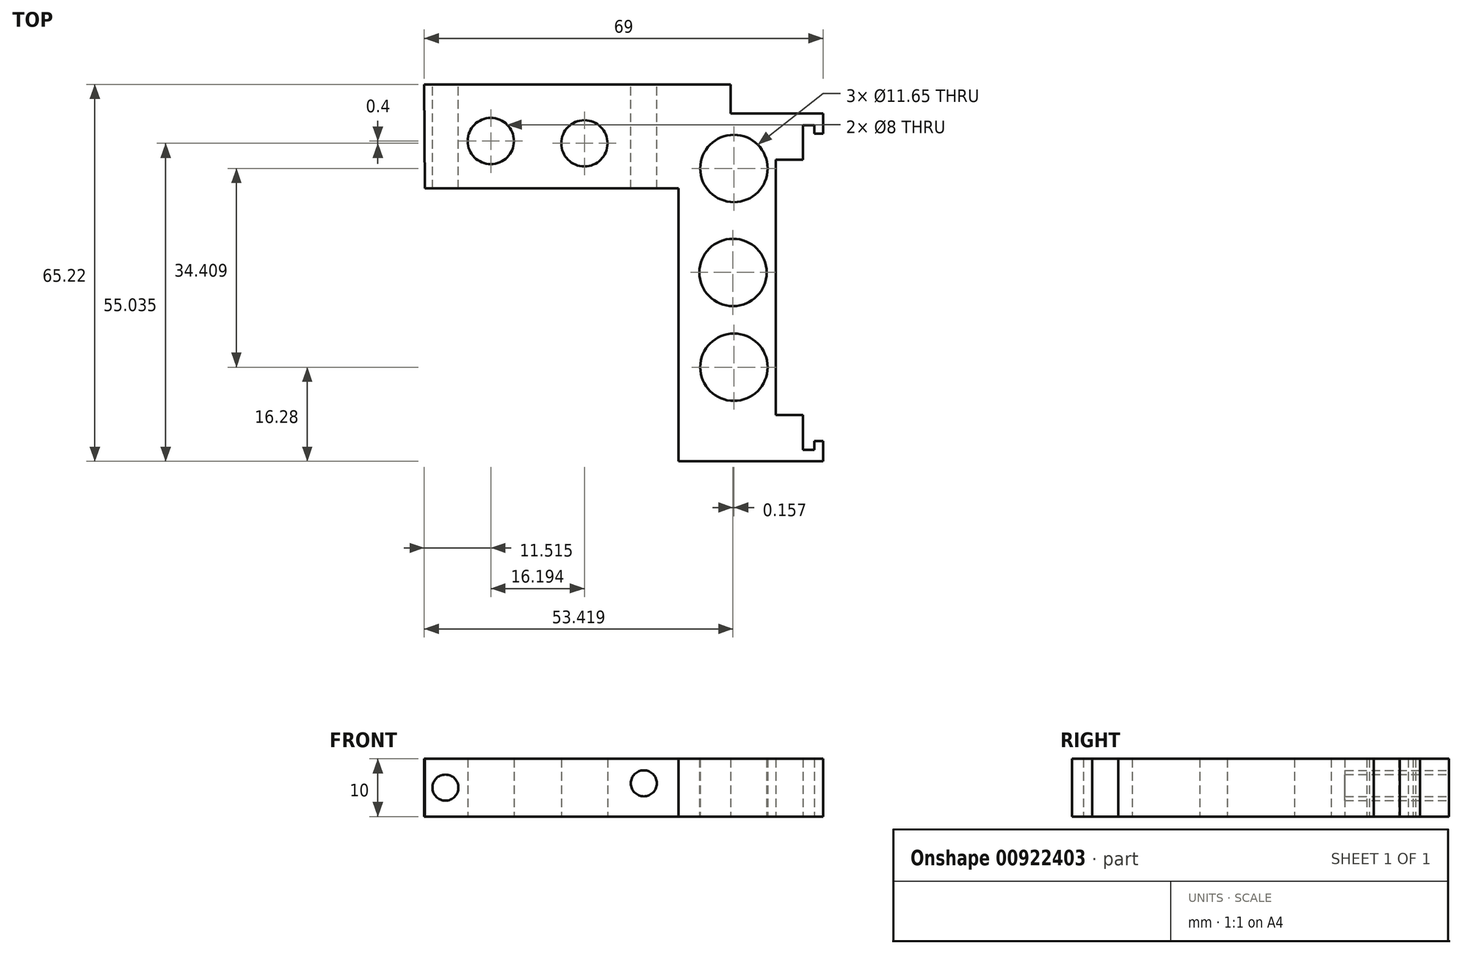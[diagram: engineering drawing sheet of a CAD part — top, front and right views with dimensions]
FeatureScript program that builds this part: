
annotation { "Feature Type Name" : "Feature", "Feature Type Description" : "" }
export const myFeature = defineFeature(function(context is Context, id is Id, definition is map)
    precondition{}
    {
        {
            var Q0;
            Q0=qCreatedBy(makeId("Top.planeOp"),FACE);
            var sketch = newSketch(context, id + "F0", { "sketchPlane" : qUnion([Q0])});
            skLineSegment(sketch, "E0.bottom", {"start": v(34, -35.12) * mm, "end": v(9, -35.12) * mm});
            skLineSegment(sketch, "E0.left", {"start": v(34, -35.12) * mm, "end": v(34, -31.62) * mm});
            skLineSegment(sketch, "E1", {"start": v(34, 21.58) * mm, "end": v(32.5, 21.58) * mm});
            skLineSegment(sketch, "E2", {"start": v(32.5, 21.58) * mm, "end": v(32.5, 23.08) * mm});
            skLineSegment(sketch, "E3", {"start": v(32.5, 23.08) * mm, "end": v(30.5, 23.08) * mm});
            skLineSegment(sketch, "E4", {"start": v(30.5, 23.08) * mm, "end": v(30.5, 17.08) * mm});
            skLineSegment(sketch, "E5", {"start": v(30.5, 17.08) * mm, "end": v(25.84, 17.08) * mm});
            skLineSegment(sketch, "E6", {"start": v(25.84, -27.12) * mm, "end": v(30.5, -27.12) * mm});
            skLineSegment(sketch, "E7", {"start": v(30.5, -33.12) * mm, "end": v(30.5, -27.12) * mm});
            skLineSegment(sketch, "E8", {"start": v(30.5, -33.12) * mm, "end": v(32.5, -33.12) * mm});
            skLineSegment(sketch, "E9", {"start": v(32.5, -33.12) * mm, "end": v(32.5, -33.12) * mm});
            skLineSegment(sketch, "E10", {"start": v(32.5, -31.62) * mm, "end": v(32.5, -33.12) * mm});
            skLineSegment(sketch, "E11", {"start": v(32.5, -31.62) * mm, "end": v(34, -31.62) * mm});
            skLineSegment(sketch, "E12.trimOffspring", {"start": v(34, 21.58) * mm, "end": v(34, 25.08) * mm});
            skLineSegment(sketch, "E13", {"start": v(-34.86, 12.1) * mm, "end": v(9, 12.1) * mm});
            skLineSegment(sketch, "E14", {"start": v(-34.86, 12.1) * mm, "end": v(-35, 30.1) * mm});
            skLineSegment(sketch, "E15", {"start": v(9, 12.1) * mm, "end": v(9, -35.12) * mm});
            skCircle(sketch, "E16", {"center": v(18.58, 15.57) * mm, "radius": 5.83 * mm});
            skCircle(sketch, "E17", {"center": v(18.42, -2.43) * mm, "radius": 5.83 * mm});
            skCircle(sketch, "E18", {"center": v(18.58, -18.84) * mm, "radius": 5.83 * mm});
            skLineSegment(sketch, "E19", {"start": v(34, 25.08) * mm, "end": v(18, 25.08) * mm});
            skLineSegment(sketch, "E20", {"start": v(18, 30.1) * mm, "end": v(18, 25.08) * mm});
            skLineSegment(sketch, "E21", {"start": v(-35, 30.1) * mm, "end": v(18, 30.1) * mm});
            skCircle(sketch, "E22", {"center": v(-23.49, 20.32) * mm, "radius": 4 * mm});
            skCircle(sketch, "E23", {"center": v(-7.3, 19.91) * mm, "radius": 4 * mm});
            skLineSegment(sketch, "E24", {"start": v(25.84, -27.12) * mm, "end": v(25.84, -27.12) * mm});
            skLineSegment(sketch, "E25", {"start": v(25.84, 17.08) * mm, "end": v(25.84, -27.12) * mm});
            skSolve(sketch);
        }
        {
            var Q0;
            Q0=makeQuery(id+"F0.imprint","IMPRINT",FACE,{"disambiguationData":[TD([[makeQuery(id+"F0.imprint","IMPRINT",EDGE,{"derivedFrom":sQuery(id+"F0.wireOp",EDGE,"E0.bottom")}),-1.0]])]});
            extrude(context, id + "F1", {"entities" : qUnion([Q0]), "depth" : 10 * mm, "offsetDistance" : 25 * mm});
        }
        {
            var Q0;
            Q0=makeQuery(id+"F1.opExtrude","SWEPT_FACE",FACE,{"disambiguationData":[OSD([sQuery(id+"F0.wireOp",EDGE,"E21")])]});
            var sketch = newSketch(context, id + "F2", { "sketchPlane" : qUnion([Q0])});
            skLineSegment(sketch, "E26", {"start": v(-18, 10) * mm, "end": v(-18, 0) * mm});
            skLineSegment(sketch, "E27", {"start": v(-18, 0) * mm, "end": v(-18, 5) * mm});
            skLineSegment(sketch, "E28", {"start": v(35, 5) * mm, "end": v(0, 5) * mm, "construction": true});
            skLineSegment(sketch, "E29", {"start": v(0, 5) * mm, "end": v(-5.98, 6.49) * mm, "construction": true});
            skLineSegment(sketch, "E30", {"start": v(-5.98, 6.49) * mm, "end": v(-15.26, 6.3) * mm, "construction": true});
            skPoint(sketch, "E31", {"position": v(-2.99, 5.74) * mm});
            skPoint(sketch, "E32", {"position": v(17.5, 5) * mm});
            skCircle(sketch, "E33", {"center": v(-2.99, 5.74) * mm, "radius": 2.25 * mm});
            skCircle(sketch, "E34", {"center": v(31.33, 5) * mm, "radius": 2.25 * mm});
            skSolve(sketch);
        }
        {
            var Q0;
            Q0 = qSketchRegion(id + "F2", true);
            extrude(context, id + "F3", {"entities" : qUnion([Q0]), "operationType" : NewBodyOperationType.REMOVE, "endBound" : BoundingType.THROUGH_ALL, "oppositeDirection" : true, "depth" : 25 * mm, "offsetDistance" : 25 * mm});
        }
    });
